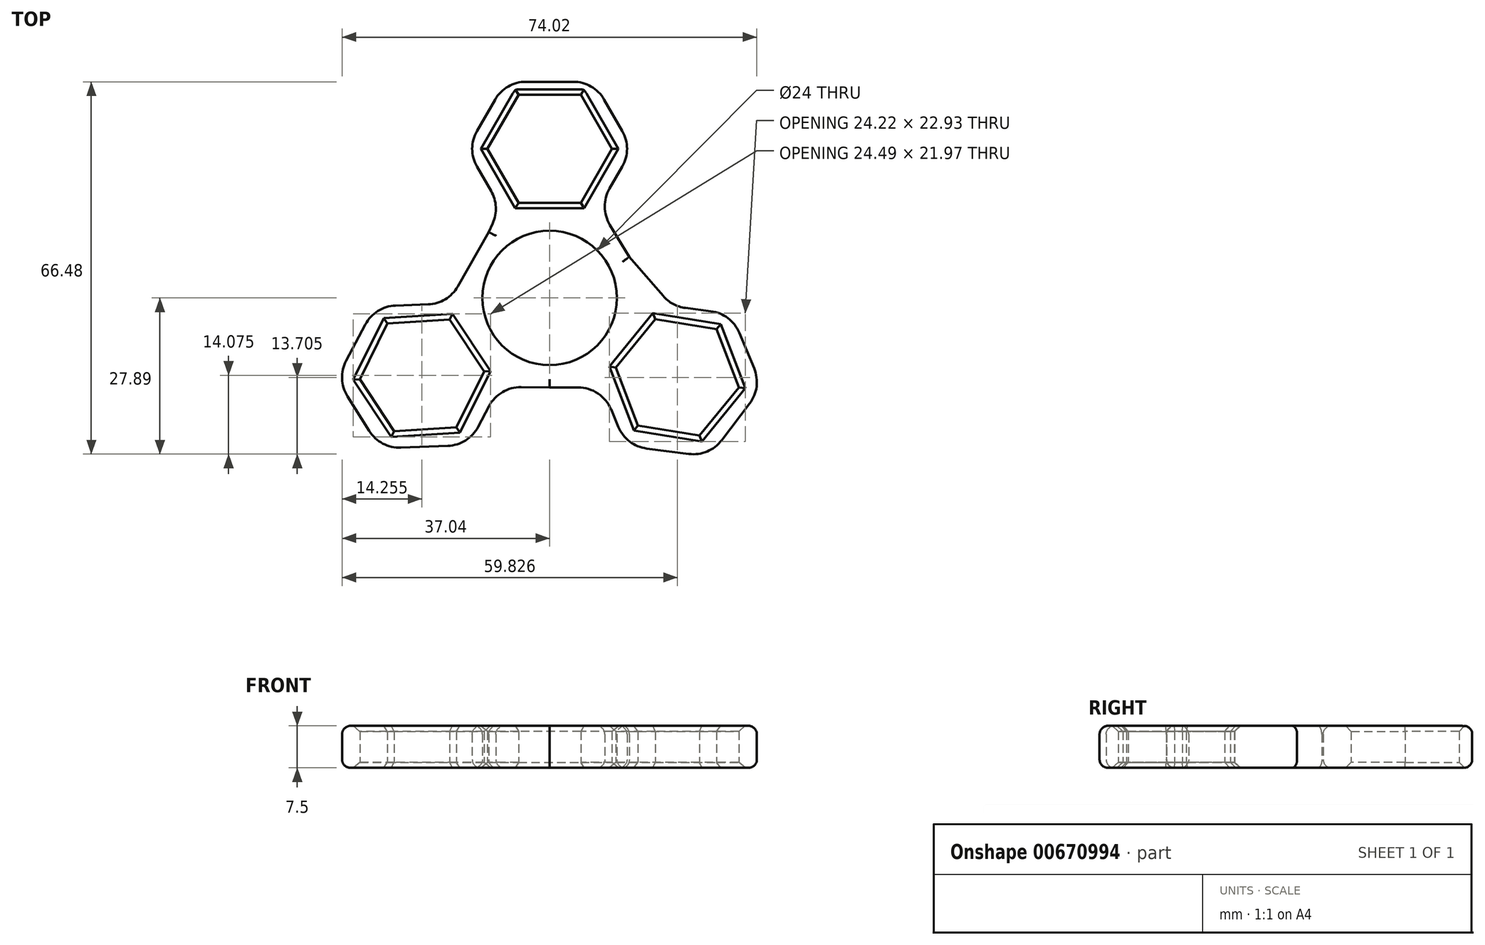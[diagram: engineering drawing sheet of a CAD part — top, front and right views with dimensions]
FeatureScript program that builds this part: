
annotation { "Feature Type Name" : "Feature", "Feature Type Description" : "" }
export const myFeature = defineFeature(function(context is Context, id is Id, definition is map)
    precondition{}
    {
        {
            var Q0;
            Q0=qCreatedBy(makeId("Top.planeOp"),FACE);
            var sketch = newSketch(context, id + "F0", { "sketchPlane" : qUnion([Q0])});
            skCircle(sketch, "E0", {"center": v(0, 0) * mm, "radius": 12 * mm});
            skCircle(sketch, "E1.cCircle", {"center": v(0, 26.62) * mm, "radius": 9.62 * mm, "construction": true});
            skLineSegment(sketch, "E1.0", {"start": v(-5.56, 36.25) * mm, "end": v(5.56, 36.25) * mm});
            skLineSegment(sketch, "E1.1", {"start": v(5.56, 36.25) * mm, "end": v(11.11, 26.62) * mm});
            skLineSegment(sketch, "E1.2", {"start": v(11.11, 26.62) * mm, "end": v(5.56, 17) * mm});
            skLineSegment(sketch, "E1.3", {"start": v(5.56, 17) * mm, "end": v(-5.56, 17) * mm});
            skLineSegment(sketch, "E1.4", {"start": v(-5.56, 17) * mm, "end": v(-11.11, 26.62) * mm});
            skLineSegment(sketch, "E1.5", {"start": v(-11.11, 26.62) * mm, "end": v(-5.56, 36.25) * mm});
            skPoint(sketch, "E1.0.midPoint", {"position": v(0, 36.25) * mm});
            skCircle(sketch, "E2.cCircle", {"center": v(22.79, -14.18) * mm, "radius": 9.62 * mm, "construction": true});
            skLineSegment(sketch, "E2.0", {"start": v(18.84, -3.8) * mm, "end": v(29.8, -5.57) * mm});
            skLineSegment(sketch, "E2.1", {"start": v(29.8, -5.57) * mm, "end": v(33.76, -15.96) * mm});
            skLineSegment(sketch, "E2.2", {"start": v(33.76, -15.96) * mm, "end": v(26.73, -24.57) * mm});
            skLineSegment(sketch, "E2.3", {"start": v(26.73, -24.57) * mm, "end": v(15.76, -22.8) * mm});
            skLineSegment(sketch, "E2.4", {"start": v(15.76, -22.8) * mm, "end": v(11.82, -12.41) * mm});
            skLineSegment(sketch, "E2.5", {"start": v(11.82, -12.41) * mm, "end": v(18.84, -3.8) * mm});
            skPoint(sketch, "E2.0.midPoint", {"position": v(24.32, -4.68) * mm});
            skCircle(sketch, "E3.cCircle", {"center": v(-22.78, -13.81) * mm, "radius": 9.62 * mm, "construction": true});
            skLineSegment(sketch, "E3.0", {"start": v(-28.93, -4.55) * mm, "end": v(-17.84, -3.86) * mm});
            skLineSegment(sketch, "E3.1", {"start": v(-17.84, -3.86) * mm, "end": v(-11.7, -13.13) * mm});
            skLineSegment(sketch, "E3.2", {"start": v(-11.7, -13.13) * mm, "end": v(-16.64, -23.08) * mm});
            skLineSegment(sketch, "E3.3", {"start": v(-16.64, -23.08) * mm, "end": v(-27.73, -23.76) * mm});
            skLineSegment(sketch, "E3.4", {"start": v(-27.73, -23.76) * mm, "end": v(-33.88, -14.5) * mm});
            skLineSegment(sketch, "E3.5", {"start": v(-33.88, -14.5) * mm, "end": v(-28.93, -4.55) * mm});
            skPoint(sketch, "E3.0.midPoint", {"position": v(-23.38, -4.2) * mm});
            skLineSegment(sketch, "E4", {"start": v(-10.86, 11.75) * mm, "end": v(-10.16, 13.3) * mm});
            skLineSegment(sketch, "E5", {"start": v(-10.45, 19.1) * mm, "end": v(-12.96, 23.45) * mm});
            skLineSegment(sketch, "E6", {"start": v(-12.96, 29.8) * mm, "end": v(-9.72, 35.42) * mm});
            skLineSegment(sketch, "E7", {"start": v(14.22, 7.34) * mm, "end": v(10.76, 13.06) * mm});
            skLineSegment(sketch, "E8", {"start": v(10.7, 19.52) * mm, "end": v(12.96, 23.45) * mm});
            skLineSegment(sketch, "E9", {"start": v(12.96, 29.8) * mm, "end": v(9.72, 35.42) * mm});
            skLineSegment(sketch, "E10", {"start": v(4.22, 38.6) * mm, "end": v(-4.22, 38.6) * mm});
            skPoint(sketch, "E11.visualSharp", {"position": v(-7.89, 38.6) * mm});
            skArc(sketch, "E11.filletArc", {"start": v(-4.22, 38.6) * mm, "mid": v(-7.4, 37.74) * mm, "end": v(-9.72, 35.42) * mm});
            skPoint(sketch, "E12.visualSharp", {"position": v(7.89, 38.6) * mm});
            skArc(sketch, "E12.filletArc", {"start": v(9.72, 35.42) * mm, "mid": v(7.4, 37.74) * mm, "end": v(4.22, 38.6) * mm});
            skPoint(sketch, "E13.visualSharp", {"position": v(14.8, 26.62) * mm});
            skArc(sketch, "E13.filletArc", {"start": v(12.96, 23.45) * mm, "mid": v(13.81, 26.62) * mm, "end": v(12.96, 29.8) * mm});
            skPoint(sketch, "E14.visualSharp", {"position": v(-14.8, 26.62) * mm});
            skArc(sketch, "E14.filletArc", {"start": v(-12.96, 29.8) * mm, "mid": v(-13.81, 26.62) * mm, "end": v(-12.96, 23.45) * mm});
            skPoint(sketch, "E15.visualSharp", {"position": v(-8.82, 16.27) * mm});
            skArc(sketch, "E15.filletArc", {"start": v(-10.16, 13.3) * mm, "mid": v(-9.6, 16.23) * mm, "end": v(-10.45, 19.1) * mm});
            skPoint(sketch, "E16.visualSharp", {"position": v(8.82, 16.27) * mm});
            skArc(sketch, "E16.filletArc", {"start": v(10.7, 19.52) * mm, "mid": v(9.84, 16.28) * mm, "end": v(10.76, 13.06) * mm});
            skLineSegment(sketch, "E17", {"start": v(0, -16) * mm, "end": v(-5.08, -15.92) * mm});
            skLineSegment(sketch, "E18", {"start": v(-10.8, -19.3) * mm, "end": v(-12.77, -23.03) * mm});
            skLineSegment(sketch, "E19", {"start": v(-18.15, -26.4) * mm, "end": v(-26.56, -26.72) * mm});
            skLineSegment(sketch, "E20", {"start": v(-10.86, 11.75) * mm, "end": v(-16.4, 2.05) * mm});
            skLineSegment(sketch, "E21", {"start": v(-21.68, -1.15) * mm, "end": v(-27.5, -1.37) * mm});
            skLineSegment(sketch, "E22", {"start": v(-32.88, -4.75) * mm, "end": v(-36.3, -11.2) * mm});
            skLineSegment(sketch, "E23", {"start": v(-36.06, -17.55) * mm, "end": v(-32.17, -23.75) * mm});
            skArc(sketch, "E24.filletArc", {"start": v(-32.17, -23.75) * mm, "mid": v(-29.76, -26) * mm, "end": v(-26.56, -26.72) * mm});
            skArc(sketch, "E25.filletArc", {"start": v(-36.3, -11.2) * mm, "mid": v(-37.03, -14.41) * mm, "end": v(-36.06, -17.55) * mm});
            skArc(sketch, "E26.filletArc", {"start": v(-27.5, -1.37) * mm, "mid": v(-30.64, -2.34) * mm, "end": v(-32.88, -4.75) * mm});
            skArc(sketch, "E27.filletArc", {"start": v(-18.15, -26.4) * mm, "mid": v(-15, -25.44) * mm, "end": v(-12.77, -23.03) * mm});
            skArc(sketch, "E28.filletArc", {"start": v(-5.08, -15.92) * mm, "mid": v(-8.41, -16.8) * mm, "end": v(-10.8, -19.3) * mm});
            skArc(sketch, "E29.filletArc", {"start": v(-21.68, -1.15) * mm, "mid": v(-18.62, -0.24) * mm, "end": v(-16.4, 2.05) * mm});
            skLineSegment(sketch, "E30", {"start": v(14.22, 7.34) * mm, "end": v(20.24, 0.37) * mm});
            skLineSegment(sketch, "E31", {"start": v(24.24, -1.78) * mm, "end": v(28.78, -2.36) * mm});
            skLineSegment(sketch, "E32", {"start": v(33.83, -6.21) * mm, "end": v(36.49, -12.57) * mm});
            skLineSegment(sketch, "E33", {"start": v(0, -16) * mm, "end": v(5.08, -15.98) * mm});
            skLineSegment(sketch, "E34", {"start": v(10.96, -19.88) * mm, "end": v(12.27, -23.03) * mm});
            skLineSegment(sketch, "E35", {"start": v(17.32, -26.88) * mm, "end": v(24.85, -27.84) * mm});
            skLineSegment(sketch, "E36", {"start": v(30.7, -25.4) * mm, "end": v(35.68, -18.87) * mm});
            skArc(sketch, "E37.filletArc", {"start": v(35.68, -18.87) * mm, "mid": v(36.93, -15.83) * mm, "end": v(36.49, -12.57) * mm});
            skArc(sketch, "E38.filletArc", {"start": v(24.85, -27.84) * mm, "mid": v(28.1, -27.4) * mm, "end": v(30.7, -25.4) * mm});
            skArc(sketch, "E39.filletArc", {"start": v(12.27, -23.03) * mm, "mid": v(14.28, -25.63) * mm, "end": v(17.32, -26.88) * mm});
            skArc(sketch, "E40.filletArc", {"start": v(33.83, -6.21) * mm, "mid": v(31.82, -3.61) * mm, "end": v(28.78, -2.36) * mm});
            skArc(sketch, "E41.filletArc", {"start": v(20.24, 0.37) * mm, "mid": v(22.04, -1.08) * mm, "end": v(24.24, -1.78) * mm});
            skArc(sketch, "E42.filletArc", {"start": v(10.96, -19.88) * mm, "mid": v(8.61, -17.04) * mm, "end": v(5.08, -15.98) * mm});
            skSolve(sketch);
        }
        {
            var Q0;
            Q0=makeQuery(id+"F0.imprint","IMPRINT",FACE,{"disambiguationData":[TD([[makeQuery(id+"F0.imprint","IMPRINT",EDGE,{"derivedFrom":sQuery(id+"F0.wireOp",EDGE,"E0")}),-1.0]])]});
            extrude(context, id + "F1", {"entities" : qUnion([Q0]), "depth" : 7.5 * mm, "offsetDistance" : 25.4 * mm});
        }
        {
            var Q0;
            Q0=makeQuery(id+"F1.opExtrude","CAP_EDGE",EDGE,{"disambiguationData":[OSD([sQuery(id+"F0.wireOp",EDGE,"E20")])],"isStart":false});
            var Q1;
            Q1=makeQuery(id+"F1.opExtrude","CAP_EDGE",EDGE,{"disambiguationData":[OSD([sQuery(id+"F0.wireOp",EDGE,"E4")])],"isStart":false});
            var Q2;
            Q2=makeQuery(id+"F1.opExtrude","CAP_EDGE",EDGE,{"disambiguationData":[OSD([sQuery(id+"F0.wireOp",EDGE,"E15.filletArc")])],"isStart":false});
            var Q3;
            Q3=makeQuery(id+"F1.opExtrude","CAP_EDGE",EDGE,{"disambiguationData":[OSD([sQuery(id+"F0.wireOp",EDGE,"E5")])],"isStart":false});
            var Q4;
            Q4=makeQuery(id+"F1.opExtrude","CAP_EDGE",EDGE,{"disambiguationData":[OSD([sQuery(id+"F0.wireOp",EDGE,"E14.filletArc")])],"isStart":false});
            var Q5;
            Q5=makeQuery(id+"F1.opExtrude","CAP_EDGE",EDGE,{"disambiguationData":[OSD([sQuery(id+"F0.wireOp",EDGE,"E6")])],"isStart":false});
            var Q6;
            Q6=makeQuery(id+"F1.opExtrude","CAP_EDGE",EDGE,{"disambiguationData":[OSD([sQuery(id+"F0.wireOp",EDGE,"E11.filletArc")])],"isStart":false});
            var Q7;
            Q7=makeQuery(id+"F1.opExtrude","CAP_EDGE",EDGE,{"disambiguationData":[OSD([sQuery(id+"F0.wireOp",EDGE,"E10")])],"isStart":false});
            var Q8;
            Q8=makeQuery(id+"F1.opExtrude","CAP_EDGE",EDGE,{"disambiguationData":[OSD([sQuery(id+"F0.wireOp",EDGE,"E12.filletArc")])],"isStart":false});
            var Q9;
            Q9=makeQuery(id+"F1.opExtrude","CAP_EDGE",EDGE,{"disambiguationData":[OSD([sQuery(id+"F0.wireOp",EDGE,"E9")])],"isStart":false});
            var Q10;
            Q10=makeQuery(id+"F1.opExtrude","CAP_EDGE",EDGE,{"disambiguationData":[OSD([sQuery(id+"F0.wireOp",EDGE,"E13.filletArc")])],"isStart":false});
            var Q11;
            Q11=makeQuery(id+"F1.opExtrude","CAP_EDGE",EDGE,{"disambiguationData":[OSD([sQuery(id+"F0.wireOp",EDGE,"E8")])],"isStart":false});
            var Q12;
            Q12=makeQuery(id+"F1.opExtrude","CAP_EDGE",EDGE,{"disambiguationData":[OSD([sQuery(id+"F0.wireOp",EDGE,"E16.filletArc")])],"isStart":false});
            var Q13;
            Q13=makeQuery(id+"F1.opExtrude","CAP_EDGE",EDGE,{"disambiguationData":[OSD([sQuery(id+"F0.wireOp",EDGE,"E7")])],"isStart":false});
            var Q14;
            Q14=makeQuery(id+"F1.opExtrude","CAP_EDGE",EDGE,{"disambiguationData":[OSD([sQuery(id+"F0.wireOp",EDGE,"E30")])],"isStart":false});
            var Q15;
            Q15=makeQuery(id+"F1.opExtrude","CAP_EDGE",EDGE,{"disambiguationData":[OSD([sQuery(id+"F0.wireOp",EDGE,"E41.filletArc")])],"isStart":false});
            var Q16;
            Q16=makeQuery(id+"F1.opExtrude","CAP_EDGE",EDGE,{"disambiguationData":[OSD([sQuery(id+"F0.wireOp",EDGE,"E31")])],"isStart":false});
            var Q17;
            Q17=makeQuery(id+"F1.opExtrude","CAP_EDGE",EDGE,{"disambiguationData":[OSD([sQuery(id+"F0.wireOp",EDGE,"E40.filletArc")])],"isStart":false});
            var Q18;
            Q18=makeQuery(id+"F1.opExtrude","CAP_EDGE",EDGE,{"disambiguationData":[OSD([sQuery(id+"F0.wireOp",EDGE,"E32")])],"isStart":false});
            var Q19;
            Q19=makeQuery(id+"F1.opExtrude","CAP_EDGE",EDGE,{"disambiguationData":[OSD([sQuery(id+"F0.wireOp",EDGE,"E37.filletArc")])],"isStart":false});
            var Q20;
            Q20=makeQuery(id+"F1.opExtrude","CAP_EDGE",EDGE,{"disambiguationData":[OSD([sQuery(id+"F0.wireOp",EDGE,"E36")])],"isStart":false});
            var Q21;
            Q21=makeQuery(id+"F1.opExtrude","CAP_EDGE",EDGE,{"disambiguationData":[OSD([sQuery(id+"F0.wireOp",EDGE,"E38.filletArc")])],"isStart":false});
            var Q22;
            Q22=makeQuery(id+"F1.opExtrude","CAP_EDGE",EDGE,{"disambiguationData":[OSD([sQuery(id+"F0.wireOp",EDGE,"E35")])],"isStart":false});
            var Q23;
            Q23=makeQuery(id+"F1.opExtrude","CAP_EDGE",EDGE,{"disambiguationData":[OSD([sQuery(id+"F0.wireOp",EDGE,"E39.filletArc")])],"isStart":false});
            var Q24;
            Q24=makeQuery(id+"F1.opExtrude","CAP_EDGE",EDGE,{"disambiguationData":[OSD([sQuery(id+"F0.wireOp",EDGE,"E34")])],"isStart":false});
            var Q25;
            Q25=makeQuery(id+"F1.opExtrude","CAP_EDGE",EDGE,{"disambiguationData":[OSD([sQuery(id+"F0.wireOp",EDGE,"E42.filletArc")])],"isStart":false});
            var Q26;
            Q26=makeQuery(id+"F1.opExtrude","CAP_EDGE",EDGE,{"disambiguationData":[OSD([sQuery(id+"F0.wireOp",EDGE,"E33")])],"isStart":false});
            var Q27;
            Q27=makeQuery(id+"F1.opExtrude","CAP_EDGE",EDGE,{"disambiguationData":[OSD([sQuery(id+"F0.wireOp",EDGE,"E17")])],"isStart":false});
            var Q28;
            Q28=makeQuery(id+"F1.opExtrude","CAP_EDGE",EDGE,{"disambiguationData":[OSD([sQuery(id+"F0.wireOp",EDGE,"E28.filletArc")])],"isStart":false});
            var Q29;
            Q29=makeQuery(id+"F1.opExtrude","CAP_EDGE",EDGE,{"disambiguationData":[OSD([sQuery(id+"F0.wireOp",EDGE,"E18")])],"isStart":false});
            var Q30;
            Q30=makeQuery(id+"F1.opExtrude","CAP_EDGE",EDGE,{"disambiguationData":[OSD([sQuery(id+"F0.wireOp",EDGE,"E27.filletArc")])],"isStart":false});
            var Q31;
            Q31=makeQuery(id+"F1.opExtrude","CAP_EDGE",EDGE,{"disambiguationData":[OSD([sQuery(id+"F0.wireOp",EDGE,"E19")])],"isStart":false});
            var Q32;
            Q32=makeQuery(id+"F1.opExtrude","CAP_EDGE",EDGE,{"disambiguationData":[OSD([sQuery(id+"F0.wireOp",EDGE,"E24.filletArc")])],"isStart":false});
            var Q33;
            Q33=makeQuery(id+"F1.opExtrude","CAP_EDGE",EDGE,{"disambiguationData":[OSD([sQuery(id+"F0.wireOp",EDGE,"E23")])],"isStart":false});
            var Q34;
            Q34=makeQuery(id+"F1.opExtrude","CAP_EDGE",EDGE,{"disambiguationData":[OSD([sQuery(id+"F0.wireOp",EDGE,"E25.filletArc")])],"isStart":false});
            var Q35;
            Q35=makeQuery(id+"F1.opExtrude","CAP_EDGE",EDGE,{"disambiguationData":[OSD([sQuery(id+"F0.wireOp",EDGE,"E22")])],"isStart":false});
            var Q36;
            Q36=makeQuery(id+"F1.opExtrude","CAP_EDGE",EDGE,{"disambiguationData":[OSD([sQuery(id+"F0.wireOp",EDGE,"E26.filletArc")])],"isStart":false});
            var Q37;
            Q37=makeQuery(id+"F1.opExtrude","CAP_EDGE",EDGE,{"disambiguationData":[OSD([sQuery(id+"F0.wireOp",EDGE,"E21")])],"isStart":false});
            var Q38;
            Q38=makeQuery(id+"F1.opExtrude","CAP_EDGE",EDGE,{"disambiguationData":[OSD([sQuery(id+"F0.wireOp",EDGE,"E29.filletArc")])],"isStart":false});
            var Q39;
            Q39=makeQuery(id+"F1.opExtrude","CAP_EDGE",EDGE,{"disambiguationData":[OSD([sQuery(id+"F0.wireOp",EDGE,"E22")])],"isStart":true});
            var Q40;
            Q40=makeQuery(id+"F1.opExtrude","CAP_EDGE",EDGE,{"disambiguationData":[OSD([sQuery(id+"F0.wireOp",EDGE,"E25.filletArc")])],"isStart":true});
            var Q41;
            Q41=makeQuery(id+"F1.opExtrude","CAP_EDGE",EDGE,{"disambiguationData":[OSD([sQuery(id+"F0.wireOp",EDGE,"E23")])],"isStart":true});
            var Q42;
            Q42=makeQuery(id+"F1.opExtrude","CAP_EDGE",EDGE,{"disambiguationData":[OSD([sQuery(id+"F0.wireOp",EDGE,"E24.filletArc")])],"isStart":true});
            var Q43;
            Q43=makeQuery(id+"F1.opExtrude","CAP_EDGE",EDGE,{"disambiguationData":[OSD([sQuery(id+"F0.wireOp",EDGE,"E19")])],"isStart":true});
            var Q44;
            Q44=makeQuery(id+"F1.opExtrude","CAP_EDGE",EDGE,{"disambiguationData":[OSD([sQuery(id+"F0.wireOp",EDGE,"E27.filletArc")])],"isStart":true});
            var Q45;
            Q45=makeQuery(id+"F1.opExtrude","CAP_EDGE",EDGE,{"disambiguationData":[OSD([sQuery(id+"F0.wireOp",EDGE,"E18")])],"isStart":true});
            var Q46;
            Q46=makeQuery(id+"F1.opExtrude","CAP_EDGE",EDGE,{"disambiguationData":[OSD([sQuery(id+"F0.wireOp",EDGE,"E28.filletArc")])],"isStart":true});
            var Q47;
            Q47=makeQuery(id+"F1.opExtrude","CAP_EDGE",EDGE,{"disambiguationData":[OSD([sQuery(id+"F0.wireOp",EDGE,"E17")])],"isStart":true});
            var Q48;
            Q48=makeQuery(id+"F1.opExtrude","CAP_EDGE",EDGE,{"disambiguationData":[OSD([sQuery(id+"F0.wireOp",EDGE,"E33")])],"isStart":true});
            var Q49;
            Q49=makeQuery(id+"F1.opExtrude","CAP_EDGE",EDGE,{"disambiguationData":[OSD([sQuery(id+"F0.wireOp",EDGE,"E42.filletArc")])],"isStart":true});
            var Q50;
            Q50=makeQuery(id+"F1.opExtrude","CAP_EDGE",EDGE,{"disambiguationData":[OSD([sQuery(id+"F0.wireOp",EDGE,"E34")])],"isStart":true});
            var Q51;
            Q51=makeQuery(id+"F1.opExtrude","CAP_EDGE",EDGE,{"disambiguationData":[OSD([sQuery(id+"F0.wireOp",EDGE,"E39.filletArc")])],"isStart":true});
            var Q52;
            Q52=makeQuery(id+"F1.opExtrude","CAP_EDGE",EDGE,{"disambiguationData":[OSD([sQuery(id+"F0.wireOp",EDGE,"E35")])],"isStart":true});
            var Q53;
            Q53=makeQuery(id+"F1.opExtrude","CAP_EDGE",EDGE,{"disambiguationData":[OSD([sQuery(id+"F0.wireOp",EDGE,"E38.filletArc")])],"isStart":true});
            var Q54;
            Q54=makeQuery(id+"F1.opExtrude","CAP_EDGE",EDGE,{"disambiguationData":[OSD([sQuery(id+"F0.wireOp",EDGE,"E36")])],"isStart":true});
            var Q55;
            Q55=makeQuery(id+"F1.opExtrude","CAP_EDGE",EDGE,{"disambiguationData":[OSD([sQuery(id+"F0.wireOp",EDGE,"E37.filletArc")])],"isStart":true});
            var Q56;
            Q56=makeQuery(id+"F1.opExtrude","CAP_EDGE",EDGE,{"disambiguationData":[OSD([sQuery(id+"F0.wireOp",EDGE,"E32")])],"isStart":true});
            var Q57;
            Q57=makeQuery(id+"F1.opExtrude","CAP_EDGE",EDGE,{"disambiguationData":[OSD([sQuery(id+"F0.wireOp",EDGE,"E40.filletArc")])],"isStart":true});
            var Q58;
            Q58=makeQuery(id+"F1.opExtrude","CAP_EDGE",EDGE,{"disambiguationData":[OSD([sQuery(id+"F0.wireOp",EDGE,"E31")])],"isStart":true});
            var Q59;
            Q59=makeQuery(id+"F1.opExtrude","CAP_EDGE",EDGE,{"disambiguationData":[OSD([sQuery(id+"F0.wireOp",EDGE,"E41.filletArc")])],"isStart":true});
            var Q60;
            Q60=makeQuery(id+"F1.opExtrude","CAP_EDGE",EDGE,{"disambiguationData":[OSD([sQuery(id+"F0.wireOp",EDGE,"E30")])],"isStart":true});
            var Q61;
            Q61=makeQuery(id+"F1.opExtrude","CAP_EDGE",EDGE,{"disambiguationData":[OSD([sQuery(id+"F0.wireOp",EDGE,"E7")])],"isStart":true});
            var Q62;
            Q62=makeQuery(id+"F1.opExtrude","CAP_EDGE",EDGE,{"disambiguationData":[OSD([sQuery(id+"F0.wireOp",EDGE,"E16.filletArc")])],"isStart":true});
            var Q63;
            Q63=makeQuery(id+"F1.opExtrude","CAP_EDGE",EDGE,{"disambiguationData":[OSD([sQuery(id+"F0.wireOp",EDGE,"E8")])],"isStart":true});
            var Q64;
            Q64=makeQuery(id+"F1.opExtrude","CAP_EDGE",EDGE,{"disambiguationData":[OSD([sQuery(id+"F0.wireOp",EDGE,"E13.filletArc")])],"isStart":true});
            var Q65;
            Q65=makeQuery(id+"F1.opExtrude","CAP_EDGE",EDGE,{"disambiguationData":[OSD([sQuery(id+"F0.wireOp",EDGE,"E9")])],"isStart":true});
            var Q66;
            Q66=makeQuery(id+"F1.opExtrude","CAP_EDGE",EDGE,{"disambiguationData":[OSD([sQuery(id+"F0.wireOp",EDGE,"E12.filletArc")])],"isStart":true});
            var Q67;
            Q67=makeQuery(id+"F1.opExtrude","CAP_EDGE",EDGE,{"disambiguationData":[OSD([sQuery(id+"F0.wireOp",EDGE,"E10")])],"isStart":true});
            var Q68;
            Q68=makeQuery(id+"F1.opExtrude","CAP_EDGE",EDGE,{"disambiguationData":[OSD([sQuery(id+"F0.wireOp",EDGE,"E11.filletArc")])],"isStart":true});
            var Q69;
            Q69=makeQuery(id+"F1.opExtrude","CAP_EDGE",EDGE,{"disambiguationData":[OSD([sQuery(id+"F0.wireOp",EDGE,"E6")])],"isStart":true});
            var Q70;
            Q70=makeQuery(id+"F1.opExtrude","CAP_EDGE",EDGE,{"disambiguationData":[OSD([sQuery(id+"F0.wireOp",EDGE,"E14.filletArc")])],"isStart":true});
            var Q71;
            Q71=makeQuery(id+"F1.opExtrude","CAP_EDGE",EDGE,{"disambiguationData":[OSD([sQuery(id+"F0.wireOp",EDGE,"E5")])],"isStart":true});
            var Q72;
            Q72=makeQuery(id+"F1.opExtrude","CAP_EDGE",EDGE,{"disambiguationData":[OSD([sQuery(id+"F0.wireOp",EDGE,"E15.filletArc")])],"isStart":true});
            var Q73;
            Q73=makeQuery(id+"F1.opExtrude","CAP_EDGE",EDGE,{"disambiguationData":[OSD([sQuery(id+"F0.wireOp",EDGE,"E4")])],"isStart":true});
            var Q74;
            Q74=makeQuery(id+"F1.opExtrude","CAP_EDGE",EDGE,{"disambiguationData":[OSD([sQuery(id+"F0.wireOp",EDGE,"E20")])],"isStart":true});
            var Q75;
            Q75=makeQuery(id+"F1.opExtrude","CAP_EDGE",EDGE,{"disambiguationData":[OSD([sQuery(id+"F0.wireOp",EDGE,"E29.filletArc")])],"isStart":true});
            var Q76;
            Q76=makeQuery(id+"F1.opExtrude","CAP_EDGE",EDGE,{"disambiguationData":[OSD([sQuery(id+"F0.wireOp",EDGE,"E26.filletArc")])],"isStart":true});
            var Q77;
            Q77=makeQuery(id+"F1.opExtrude","CAP_EDGE",EDGE,{"disambiguationData":[OSD([sQuery(id+"F0.wireOp",EDGE,"E21")])],"isStart":true});
            fillet(context, id + "F2", {"entities" : qUnion([Q0, Q1, Q2, Q3, Q4, Q5, Q6, Q7, Q8, Q9, Q10, Q11, Q12, Q13, Q14, Q15, Q16, Q17, Q18, Q19, Q20, Q21, Q22, Q23, Q24, Q25, Q26, Q27, Q28, Q29, Q30, Q31, Q32, Q33, Q34, Q35, Q36, Q37, Q38, Q39, Q40, Q41, Q42, Q43, Q44, Q45, Q46, Q47, Q48, Q49, Q50, Q51, Q52, Q53, Q54, Q55, Q56, Q57, Q58, Q59, Q60, Q61, Q62, Q63, Q64, Q65, Q66, Q67, Q68, Q69, Q70, Q71, Q72, Q73, Q74, Q75, Q76, Q77]), "radius" : 1.5 * mm, "tangentPropagation" : true, "allowEdgeOverflow" : false});
        }
        {
            var Q0;
            Q0=makeQuery(id+"F1.opExtrude","CAP_EDGE",EDGE,{"disambiguationData":[OSD([sQuery(id+"F0.wireOp",EDGE,"E0")])],"isStart":true});
            var Q1;
            Q1=makeQuery(id+"F1.opExtrude","CAP_EDGE",EDGE,{"disambiguationData":[OSD([sQuery(id+"F0.wireOp",EDGE,"E0")])],"isStart":false});
            fillet(context, id + "F3", {"entities" : qUnion([Q0, Q1]), "radius" : 1.5 * mm, "tangentPropagation" : true, "allowEdgeOverflow" : false});
        }
        {
            var Q0;
            Q0=makeQuery(id+"F1.opExtrude","CAP_EDGE",EDGE,{"disambiguationData":[OSD([sQuery(id+"F0.wireOp",EDGE,"E3.5")])],"isStart":false});
            var Q1;
            Q1=makeQuery(id+"F1.opExtrude","CAP_EDGE",EDGE,{"disambiguationData":[OSD([sQuery(id+"F0.wireOp",EDGE,"E3.4")])],"isStart":false});
            var Q2;
            Q2=makeQuery(id+"F1.opExtrude","CAP_EDGE",EDGE,{"disambiguationData":[OSD([sQuery(id+"F0.wireOp",EDGE,"E3.3")])],"isStart":false});
            var Q3;
            Q3=makeQuery(id+"F1.opExtrude","CAP_EDGE",EDGE,{"disambiguationData":[OSD([sQuery(id+"F0.wireOp",EDGE,"E3.2")])],"isStart":false});
            var Q4;
            Q4=makeQuery(id+"F1.opExtrude","CAP_EDGE",EDGE,{"disambiguationData":[OSD([sQuery(id+"F0.wireOp",EDGE,"E3.1")])],"isStart":false});
            var Q5;
            Q5=makeQuery(id+"F1.opExtrude","CAP_EDGE",EDGE,{"disambiguationData":[OSD([sQuery(id+"F0.wireOp",EDGE,"E3.0")])],"isStart":false});
            var Q6;
            Q6=makeQuery(id+"F1.opExtrude","CAP_EDGE",EDGE,{"disambiguationData":[OSD([sQuery(id+"F0.wireOp",EDGE,"E1.4")])],"isStart":false});
            var Q7;
            Q7=makeQuery(id+"F1.opExtrude","CAP_EDGE",EDGE,{"disambiguationData":[OSD([sQuery(id+"F0.wireOp",EDGE,"E1.5")])],"isStart":false});
            var Q8;
            Q8=makeQuery(id+"F1.opExtrude","CAP_EDGE",EDGE,{"disambiguationData":[OSD([sQuery(id+"F0.wireOp",EDGE,"E1.0")])],"isStart":false});
            var Q9;
            Q9=makeQuery(id+"F1.opExtrude","CAP_EDGE",EDGE,{"disambiguationData":[OSD([sQuery(id+"F0.wireOp",EDGE,"E1.1")])],"isStart":false});
            var Q10;
            Q10=makeQuery(id+"F1.opExtrude","CAP_EDGE",EDGE,{"disambiguationData":[OSD([sQuery(id+"F0.wireOp",EDGE,"E1.2")])],"isStart":false});
            var Q11;
            Q11=makeQuery(id+"F1.opExtrude","CAP_EDGE",EDGE,{"disambiguationData":[OSD([sQuery(id+"F0.wireOp",EDGE,"E1.3")])],"isStart":false});
            var Q12;
            Q12=makeQuery(id+"F1.opExtrude","CAP_EDGE",EDGE,{"disambiguationData":[OSD([sQuery(id+"F0.wireOp",EDGE,"E2.5")])],"isStart":false});
            var Q13;
            Q13=makeQuery(id+"F1.opExtrude","CAP_EDGE",EDGE,{"disambiguationData":[OSD([sQuery(id+"F0.wireOp",EDGE,"E2.0")])],"isStart":false});
            var Q14;
            Q14=makeQuery(id+"F1.opExtrude","CAP_EDGE",EDGE,{"disambiguationData":[OSD([sQuery(id+"F0.wireOp",EDGE,"E2.1")])],"isStart":false});
            var Q15;
            Q15=makeQuery(id+"F1.opExtrude","CAP_EDGE",EDGE,{"disambiguationData":[OSD([sQuery(id+"F0.wireOp",EDGE,"E2.2")])],"isStart":false});
            var Q16;
            Q16=makeQuery(id+"F1.opExtrude","CAP_EDGE",EDGE,{"disambiguationData":[OSD([sQuery(id+"F0.wireOp",EDGE,"E2.3")])],"isStart":false});
            var Q17;
            Q17=makeQuery(id+"F1.opExtrude","CAP_EDGE",EDGE,{"disambiguationData":[OSD([sQuery(id+"F0.wireOp",EDGE,"E2.4")])],"isStart":false});
            var Q18;
            Q18=makeQuery(id+"F1.opExtrude","CAP_EDGE",EDGE,{"disambiguationData":[OSD([sQuery(id+"F0.wireOp",EDGE,"E2.5")])],"isStart":true});
            var Q19;
            Q19=makeQuery(id+"F1.opExtrude","CAP_EDGE",EDGE,{"disambiguationData":[OSD([sQuery(id+"F0.wireOp",EDGE,"E2.4")])],"isStart":true});
            var Q20;
            Q20=makeQuery(id+"F1.opExtrude","CAP_EDGE",EDGE,{"disambiguationData":[OSD([sQuery(id+"F0.wireOp",EDGE,"E2.3")])],"isStart":true});
            var Q21;
            Q21=makeQuery(id+"F1.opExtrude","CAP_EDGE",EDGE,{"disambiguationData":[OSD([sQuery(id+"F0.wireOp",EDGE,"E2.2")])],"isStart":true});
            var Q22;
            Q22=makeQuery(id+"F1.opExtrude","CAP_EDGE",EDGE,{"disambiguationData":[OSD([sQuery(id+"F0.wireOp",EDGE,"E2.1")])],"isStart":true});
            var Q23;
            Q23=makeQuery(id+"F1.opExtrude","CAP_EDGE",EDGE,{"disambiguationData":[OSD([sQuery(id+"F0.wireOp",EDGE,"E2.0")])],"isStart":true});
            var Q24;
            Q24=makeQuery(id+"F1.opExtrude","CAP_EDGE",EDGE,{"disambiguationData":[OSD([sQuery(id+"F0.wireOp",EDGE,"E1.2")])],"isStart":true});
            var Q25;
            Q25=makeQuery(id+"F1.opExtrude","CAP_EDGE",EDGE,{"disambiguationData":[OSD([sQuery(id+"F0.wireOp",EDGE,"E1.1")])],"isStart":true});
            var Q26;
            Q26=makeQuery(id+"F1.opExtrude","CAP_EDGE",EDGE,{"disambiguationData":[OSD([sQuery(id+"F0.wireOp",EDGE,"E1.0")])],"isStart":true});
            var Q27;
            Q27=makeQuery(id+"F1.opExtrude","CAP_EDGE",EDGE,{"disambiguationData":[OSD([sQuery(id+"F0.wireOp",EDGE,"E1.5")])],"isStart":true});
            var Q28;
            Q28=makeQuery(id+"F1.opExtrude","CAP_EDGE",EDGE,{"disambiguationData":[OSD([sQuery(id+"F0.wireOp",EDGE,"E1.4")])],"isStart":true});
            var Q29;
            Q29=makeQuery(id+"F1.opExtrude","CAP_EDGE",EDGE,{"disambiguationData":[OSD([sQuery(id+"F0.wireOp",EDGE,"E1.3")])],"isStart":true});
            var Q30;
            Q30=makeQuery(id+"F1.opExtrude","CAP_EDGE",EDGE,{"disambiguationData":[OSD([sQuery(id+"F0.wireOp",EDGE,"E3.1")])],"isStart":true});
            var Q31;
            Q31=makeQuery(id+"F1.opExtrude","CAP_EDGE",EDGE,{"disambiguationData":[OSD([sQuery(id+"F0.wireOp",EDGE,"E3.0")])],"isStart":true});
            var Q32;
            Q32=makeQuery(id+"F1.opExtrude","CAP_EDGE",EDGE,{"disambiguationData":[OSD([sQuery(id+"F0.wireOp",EDGE,"E3.2")])],"isStart":true});
            var Q33;
            Q33=makeQuery(id+"F1.opExtrude","CAP_EDGE",EDGE,{"disambiguationData":[OSD([sQuery(id+"F0.wireOp",EDGE,"E3.3")])],"isStart":true});
            var Q34;
            Q34=makeQuery(id+"F1.opExtrude","CAP_EDGE",EDGE,{"disambiguationData":[OSD([sQuery(id+"F0.wireOp",EDGE,"E3.4")])],"isStart":true});
            var Q35;
            Q35=makeQuery(id+"F1.opExtrude","CAP_EDGE",EDGE,{"disambiguationData":[OSD([sQuery(id+"F0.wireOp",EDGE,"E3.5")])],"isStart":true});
            chamfer(context, id + "F4", {"entities" : qUnion([Q0, Q1, Q2, Q3, Q4, Q5, Q6, Q7, Q8, Q9, Q10, Q11, Q12, Q13, Q14, Q15, Q16, Q17, Q18, Q19, Q20, Q21, Q22, Q23, Q24, Q25, Q26, Q27, Q28, Q29, Q30, Q31, Q32, Q33, Q34, Q35]), "width" : 1 * mm, "tangentPropagation" : true});
        }
    });
